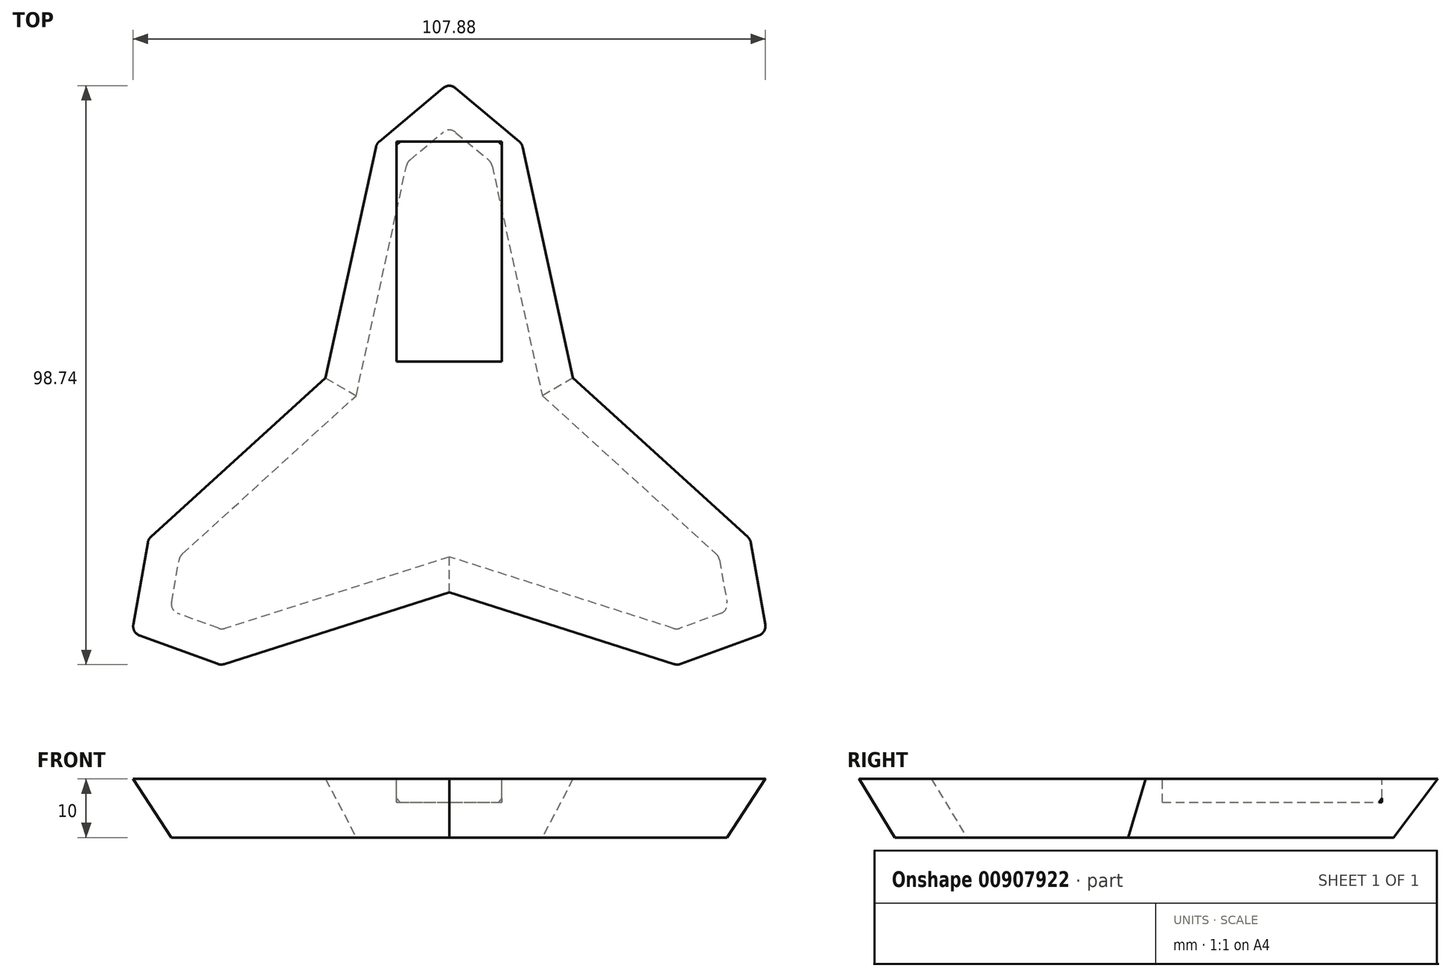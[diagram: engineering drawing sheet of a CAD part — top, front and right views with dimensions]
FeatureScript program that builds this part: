
annotation { "Feature Type Name" : "Feature", "Feature Type Description" : "" }
export const myFeature = defineFeature(function(context is Context, id is Id, definition is map)
    precondition{}
    {
        {
            var Q0;
            Q0=qCreatedBy(makeId("Top.planeOp"),FACE);
            var sketch = newSketch(context, id + "F0", { "sketchPlane" : qUnion([Q0])});
            skCircle(sketch, "E0", {"center": v(0, 0) * mm, "radius": 55 * mm, "construction": true});
            skLineSegment(sketch, "E1", {"start": v(0, 0) * mm, "end": v(-47.63, -27.5) * mm, "construction": true});
            skLineSegment(sketch, "E2", {"start": v(0, 0) * mm, "end": v(0, 55) * mm, "construction": true});
            skLineSegment(sketch, "E3", {"start": v(0, 0) * mm, "end": v(47.63, -27.5) * mm, "construction": true});
            skLineSegment(sketch, "E4", {"start": v(0, 55) * mm, "end": v(-7.18, 48.98) * mm});
            skCircle(sketch, "E5", {"center": v(0, 0) * mm, "radius": 10 * mm});
            skLineSegment(sketch, "E6", {"start": v(0, 0) * mm, "end": v(-52.94, 30.56) * mm, "construction": true});
            skLineSegment(sketch, "E7", {"start": v(0, 0) * mm, "end": v(0, -34.14) * mm, "construction": true});
            skLineSegment(sketch, "E8", {"start": v(0, 0) * mm, "end": v(50.12, 28.94) * mm, "construction": true});
            skLineSegment(sketch, "E9", {"start": v(-7.18, 48.98) * mm, "end": v(-15.88, 9.17) * mm});
            skLineSegment(sketch, "E10", {"start": v(-15.88, 9.17) * mm, "end": v(-46, -18.27) * mm});
            skLineSegment(sketch, "E11", {"start": v(-46, -18.27) * mm, "end": v(-47.63, -27.5) * mm});
            skLineSegment(sketch, "E12", {"start": v(-47.63, -27.5) * mm, "end": v(-38.83, -30.7) * mm});
            skLineSegment(sketch, "E13", {"start": v(-38.83, -30.7) * mm, "end": v(0, -18.33) * mm});
            skLineSegment(sketch, "E14", {"start": v(0, -18.33) * mm, "end": v(38.83, -30.7) * mm});
            skLineSegment(sketch, "E15", {"start": v(38.83, -30.7) * mm, "end": v(47.63, -27.5) * mm});
            skLineSegment(sketch, "E16", {"start": v(15.88, 9.17) * mm, "end": v(7.18, 48.98) * mm});
            skLineSegment(sketch, "E17", {"start": v(0, 55) * mm, "end": v(7.18, 48.98) * mm});
            skCircle(sketch, "E18", {"center": v(0, 0) * mm, "radius": 49.5 * mm, "construction": true});
            skLineSegment(sketch, "E19", {"start": v(47.63, -27.5) * mm, "end": v(46, -18.27) * mm});
            skLineSegment(sketch, "E20", {"start": v(46, -18.27) * mm, "end": v(15.88, 9.17) * mm});
            skSolve(sketch);
        }
        {
            var Q0;
            Q0=makeQuery(id+"F0.imprint","IMPRINT",FACE,{"disambiguationData":[TD([[makeQuery(id+"F0.imprint","IMPRINT",EDGE,{"derivedFrom":sQuery(id+"F0.wireOp",EDGE,"E4")}),1.0]])]});
            var Q1;
            Q1=makeQuery(id+"F0.imprint","IMPRINT",FACE,{"disambiguationData":[TD([[makeQuery(id+"F0.imprint","IMPRINT",EDGE,{"derivedFrom":sQuery(id+"F0.wireOp",EDGE,"E5")}),1.0]])]});
            extrude(context, id + "F1", {"entities" : qUnion([Q0, Q1]), "depth" : 10 * mm, "offsetDistance" : 25 * mm, "hasDraft" : true, "draftAngle" : 30 * degree});
        }
        {
            var Q0;
            Q0=makeQuery(id+"F1.opExtrude","SWEPT_EDGE",EDGE,{"disambiguationData":[OSD([sQuery(id+"F0.wireOp",EDGE,"E4"),sQuery(id+"F0.wireOp",EDGE,"E17")])]});
            var Q1;
            Q1=makeQuery(id+"F1.opExtrude","SWEPT_EDGE",EDGE,{"disambiguationData":[OSD([sQuery(id+"F0.wireOp",EDGE,"E16"),sQuery(id+"F0.wireOp",EDGE,"E17")])]});
            var Q2;
            Q2=makeQuery(id+"F1.opExtrude","SWEPT_EDGE",EDGE,{"disambiguationData":[OSD([sQuery(id+"F0.wireOp",EDGE,"E4"),sQuery(id+"F0.wireOp",EDGE,"E9")])]});
            var Q3;
            Q3=makeQuery(id+"F1.opExtrude","SWEPT_EDGE",EDGE,{"disambiguationData":[OSD([sQuery(id+"F0.wireOp",EDGE,"E19"),sQuery(id+"F0.wireOp",EDGE,"E20")])]});
            var Q4;
            Q4=makeQuery(id+"F1.opExtrude","SWEPT_EDGE",EDGE,{"disambiguationData":[OSD([sQuery(id+"F0.wireOp",EDGE,"E15"),sQuery(id+"F0.wireOp",EDGE,"E19")])]});
            var Q5;
            Q5=makeQuery(id+"F1.opExtrude","SWEPT_EDGE",EDGE,{"disambiguationData":[OSD([sQuery(id+"F0.wireOp",EDGE,"E14"),sQuery(id+"F0.wireOp",EDGE,"E15")])]});
            var Q6;
            Q6=makeQuery(id+"F1.opExtrude","SWEPT_EDGE",EDGE,{"disambiguationData":[OSD([sQuery(id+"F0.wireOp",EDGE,"E10"),sQuery(id+"F0.wireOp",EDGE,"E11")])]});
            var Q7;
            Q7=makeQuery(id+"F1.opExtrude","SWEPT_EDGE",EDGE,{"disambiguationData":[OSD([sQuery(id+"F0.wireOp",EDGE,"E11"),sQuery(id+"F0.wireOp",EDGE,"E12")])]});
            var Q8;
            Q8=makeQuery(id+"F1.opExtrude","SWEPT_EDGE",EDGE,{"disambiguationData":[OSD([sQuery(id+"F0.wireOp",EDGE,"E12"),sQuery(id+"F0.wireOp",EDGE,"E13")])]});
            fillet(context, id + "F2", {"entities" : qUnion([Q0, Q1, Q2, Q3, Q4, Q5, Q6, Q7, Q8]), "radius" : 2 * mm, "tangentPropagation" : true, "allowEdgeOverflow" : false});
        }
        {
            var Q0;
            Q0=makeQuery(id+"F1.opExtrude","CAP_FACE",FACE,{"disambiguationData":[OSD([sQuery(id+"F0.wireOp",EDGE,"E4"),sQuery(id+"F0.wireOp",EDGE,"E9"),sQuery(id+"F0.wireOp",EDGE,"E10"),sQuery(id+"F0.wireOp",EDGE,"E11"),sQuery(id+"F0.wireOp",EDGE,"E12"),sQuery(id+"F0.wireOp",EDGE,"E13"),sQuery(id+"F0.wireOp",EDGE,"E14"),sQuery(id+"F0.wireOp",EDGE,"E15"),sQuery(id+"F0.wireOp",EDGE,"E16"),sQuery(id+"F0.wireOp",EDGE,"E17"),sQuery(id+"F0.wireOp",EDGE,"E19"),sQuery(id+"F0.wireOp",EDGE,"E20")])],"isStart":false});
            var sketch = newSketch(context, id + "F3", { "sketchPlane" : qUnion([Q0])});
            skLineSegment(sketch, "E21.bottom", {"start": v(-9, 15) * mm, "end": v(9, 15) * mm});
            skLineSegment(sketch, "E21.top", {"start": v(-9, 52.5) * mm, "end": v(9, 52.5) * mm});
            skLineSegment(sketch, "E21.left", {"start": v(-9, 15) * mm, "end": v(-9, 52.5) * mm});
            skLineSegment(sketch, "E21.right", {"start": v(9, 15) * mm, "end": v(9, 52.5) * mm});
            skSolve(sketch);
        }
        {
            var Q0;
            Q0=makeQuery(id+"F3.imprint","IMPRINT",FACE,{"disambiguationData":[TD([[makeQuery(id+"F3.imprint","IMPRINT",EDGE,{"derivedFrom":sQuery(id+"F3.wireOp",EDGE,"E21.bottom")}),1.0]])]});
            extrude(context, id + "F4", {"entities" : qUnion([Q0]), "operationType" : NewBodyOperationType.REMOVE, "oppositeDirection" : true, "depth" : 4 * mm, "offsetDistance" : 25 * mm});
        }
    });
